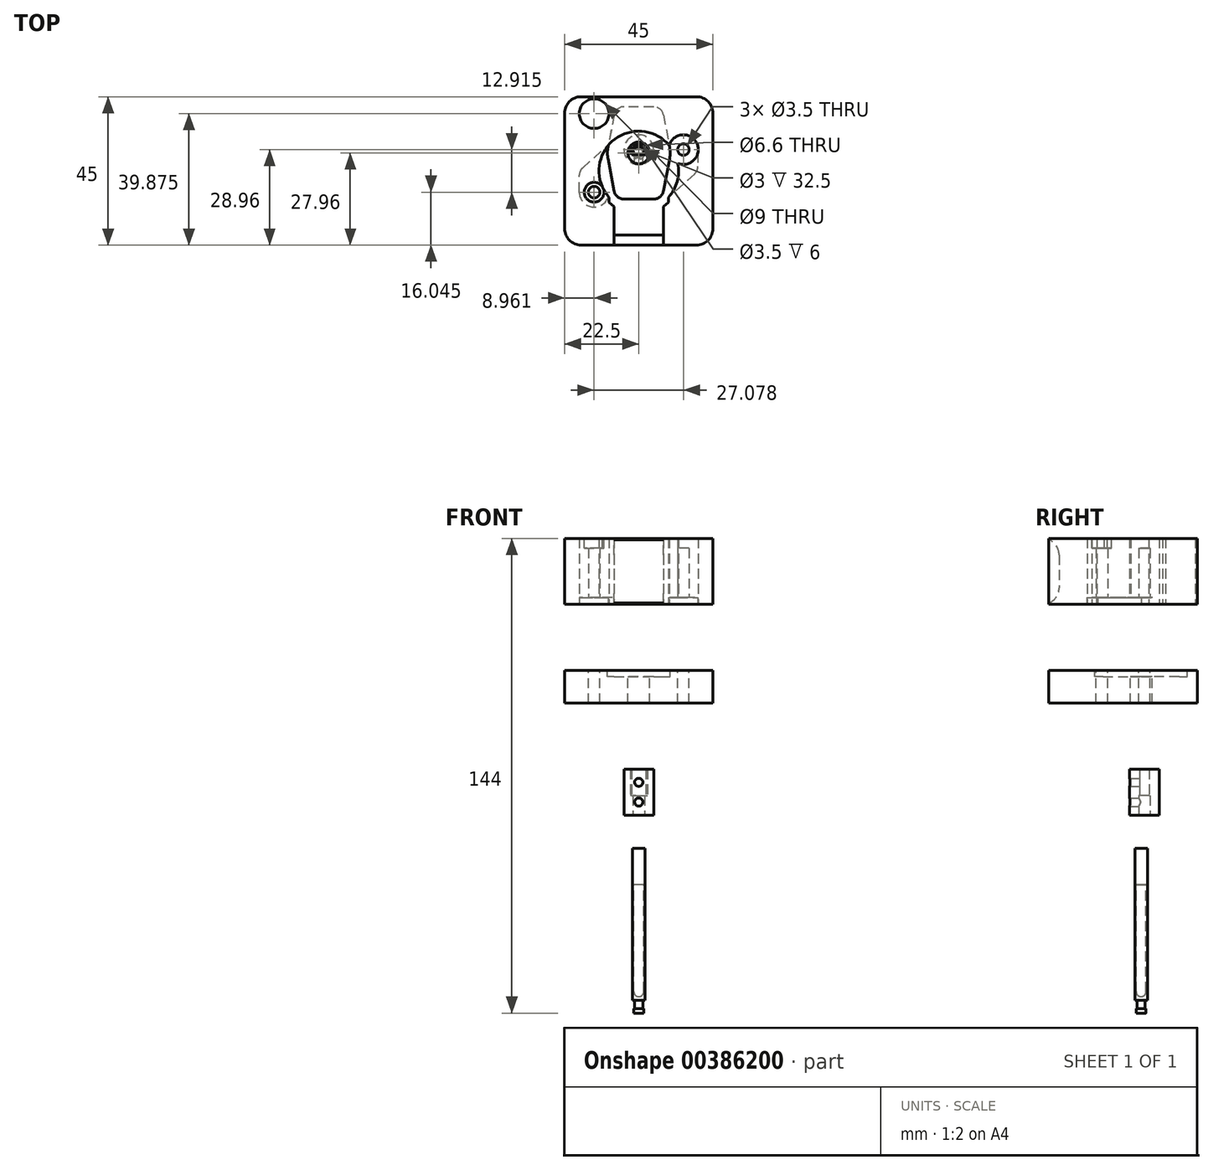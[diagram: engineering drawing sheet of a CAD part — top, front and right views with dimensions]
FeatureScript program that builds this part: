
annotation { "Feature Type Name" : "Feature", "Feature Type Description" : "" }
export const myFeature = defineFeature(function(context is Context, id is Id, definition is map)
    precondition{}
    {
        {
            assignVariable(context, id + "F0", {"name" : "plunger_h", "anyValue" : 50});
        }
        {
            assignVariable(context, id + "F1", {"name" : "M4_rivet_len", "anyValue" : 11});
        }
        {
            var Q0;
            Q0=qCreatedBy(makeId("Front.planeOp"),FACE);
            var sketch = newSketch(context, id + "F2", { "sketchPlane" : qUnion([Q0])});
            skLineSegment(sketch, "E0", {"start": v(0, 15.38) * mm, "end": v(0, -12.78) * mm, "construction": true});
            skLineSegment(sketch, "E1", {"start": v(0, 0) * mm, "end": v(1.5, 0) * mm});
            skLineSegment(sketch, "E2", {"start": v(1.5, 0) * mm, "end": v(1.5, 1.4) * mm});
            skLineSegment(sketch, "E3", {"start": v(1.5, 1.4) * mm, "end": v(1.25, 1.4) * mm});
            skLineSegment(sketch, "E4", {"start": v(1.25, 1.4) * mm, "end": v(1.25, 3.9) * mm});
            skLineSegment(sketch, "E5", {"start": v(1.25, 3.9) * mm, "end": v(1.9, 3.9) * mm});
            skLineSegment(sketch, "E6", {"start": v(1.9, 3.9) * mm, "end": v(1.9, 50) * mm});
            skLineSegment(sketch, "E7", {"start": v(1.9, 50) * mm, "end": v(1.5, 50) * mm});
            skLineSegment(sketch, "E8", {"start": v(1.5, 50) * mm, "end": v(1.5, 6.5) * mm});
            skLineSegment(sketch, "E9", {"start": v(0, 5) * mm, "end": v(0, 5) * mm});
            skLineSegment(sketch, "E10", {"start": v(0, 5) * mm, "end": v(0, 0) * mm});
            skPoint(sketch, "E11.visualSharp", {"position": v(1.5, 5) * mm});
            skArc(sketch, "E11.filletArc", {"start": v(0, 5) * mm, "mid": v(1.06, 5.44) * mm, "end": v(1.5, 6.5) * mm});
            skSolve(sketch);
        }
        {
            var Q0;
            Q0=makeQuery(id+"F2.imprint","IMPRINT",FACE,{"disambiguationData":[TD([[makeQuery(id+"F2.imprint","IMPRINT",EDGE,{"derivedFrom":sQuery(id+"F2.wireOp",EDGE,"E1")}),1.0]])]});
            var Q1;
            Q1=sQuery(id+"F2.wireOp",EDGE,"E0");
            revolve(context, id + "F3", {"entities" : qUnion([Q0]), "axis" : qUnion([Q1]), "revolveType" : RevolveType.FULL});
        }
        {
            var Q0;
            Q0=makeQuery(id+"F3.opRevolve","SWEPT_FACE",FACE,{"disambiguationData":[OSD([sQuery(id+"F2.wireOp",EDGE,"E7")])]});
            var sketch = newSketch(context, id + "F4", { "sketchPlane" : qUnion([Q0])});
            skCircle(sketch, "E12", {"center": v(0, 0) * mm, "radius": 1.5 * mm});
            skLineSegment(sketch, "E13", {"start": v(0, 11.62) * mm, "end": v(0, -12.28) * mm, "construction": true});
            skLineSegment(sketch, "E14", {"start": v(11.89, 0) * mm, "end": v(-13.02, 0) * mm, "construction": true});
            skCircle(sketch, "E15", {"center": v(0, 1) * mm, "radius": 1.75 * mm});
            skSolve(sketch);
        }
        {
            var Q0;
            Q0=makeQuery(id+"F4.imprint","IMPRINT",FACE,{"disambiguationData":[TD([[makeQuery(id+"F4.imprint","IMPRINT",EDGE,{"derivedFrom":sQuery(id+"F4.wireOp",EDGE,"E12")}),1.0]])]});
            extrude(context, id + "F5", {"entities" : qUnion([Q0]), "operationType" : NewBodyOperationType.ADD, "oppositeDirection" : true, "depth" : (getVariable(context, 'M4_rivet_len')) * mm});
        }
        {
            var Q0;
            Q0=qCreatedBy(makeId("Top.planeOp"),FACE);
            cPlane(context, id + "F6", {"entities" : qUnion([Q0]), "cplaneType" : CPlaneType.OFFSET, "offset" : (getVariable(context, 'plunger_h') + 10) * mm, "width" : 150 * mm, "height" : 150 * mm});
        }
        {
            var Q0;
            Q0=qCreatedBy(id+"F6.planeOp",FACE);
            var sketch = newSketch(context, id + "F7", { "sketchPlane" : qUnion([Q0])});
            skCircle(sketch, "E16", {"center": v(0, 1) * mm, "radius": 4.5 * mm});
            skCircle(sketch, "E17", {"center": v(0, 1) * mm, "radius": 2.6 * mm});
            skLineSegment(sketch, "E18", {"start": v(-2.12, 2.5) * mm, "end": v(2.12, 2.5) * mm});
            skLineSegment(sketch, "E19", {"start": v(-2.12, -0.5) * mm, "end": v(2.12, -0.5) * mm});
            skCircle(sketch, "E20", {"center": v(0, 1) * mm, "radius": 1.75 * mm});
            skSolve(sketch);
        }
        {
            var Q0;
            Q0=makeQuery(id+"F7.imprint","IMPRINT",FACE,{"disambiguationData":[TD([[makeQuery(id+"F7.imprint","IMPRINT",EDGE,{"derivedFrom":sQuery(id+"F7.wireOp",EDGE,"E16")}),1.0]])]});
            var Q1;
            {var subQ0=sQuery(id+"F7.wireOp",EDGE,"E19");var subQ1=sQuery(id+"F7.wireOp",EDGE,"E17");var subQ2=makeQuery(id+"F7.imprint","INTERSECT",VERTEX,{"disambiguationData":[OD(0.0)],"derivedFrom":[subQ1,subQ0]});Q1=makeQuery(id+"F7.imprint","IMPRINT",FACE,{"disambiguationData":[TD([[makeQuery(id+"F7.imprint","IMPRINT",EDGE,{"disambiguationData":[TD([[subQ2,-1.0]])],"derivedFrom":subQ1}),1.0]])]});}
            var Q2;
            {var subQ0=sQuery(id+"F7.wireOp",EDGE,"E20");var subQ1=sQuery(id+"F7.wireOp",EDGE,"E18");var subQ2=makeQuery(id+"F7.imprint","INTERSECT",VERTEX,{"disambiguationData":[OD(0.0)],"derivedFrom":[subQ1,subQ0]});Q2=makeQuery(id+"F7.imprint","IMPRINT",FACE,{"disambiguationData":[TD([[makeQuery(id+"F7.imprint","IMPRINT",EDGE,{"disambiguationData":[TD([[subQ2,-1.0]])],"derivedFrom":subQ1}),1.0]])]});}
            var Q3;
            {var subQ0=sQuery(id+"F7.wireOp",EDGE,"E20");var subQ1=sQuery(id+"F7.wireOp",EDGE,"E19");var subQ2=makeQuery(id+"F7.imprint","INTERSECT",VERTEX,{"disambiguationData":[OD(0.0)],"derivedFrom":[subQ1,subQ0]});Q3=makeQuery(id+"F7.imprint","IMPRINT",FACE,{"disambiguationData":[TD([[makeQuery(id+"F7.imprint","IMPRINT",EDGE,{"disambiguationData":[TD([[subQ2,-1.0]])],"derivedFrom":subQ1}),-1.0]])]});}
            var Q4;
            {var subQ0=sQuery(id+"F7.wireOp",EDGE,"E18");var subQ1=sQuery(id+"F7.wireOp",EDGE,"E17");var subQ2=makeQuery(id+"F7.imprint","INTERSECT",VERTEX,{"disambiguationData":[OD(0.0)],"derivedFrom":[subQ1,subQ0]});Q4=makeQuery(id+"F7.imprint","IMPRINT",FACE,{"disambiguationData":[TD([[makeQuery(id+"F7.imprint","IMPRINT",EDGE,{"disambiguationData":[TD([[subQ2,1.0]])],"derivedFrom":subQ1}),1.0]])]});}
            extrude(context, id + "F8", {"entities" : qUnion([Q0, Q1, Q2, Q3, Q4]), "depth" : 14 * mm});
        }
        {
            var Q0;
            {var subQ0=sQuery(id+"F7.wireOp",EDGE,"E18");var subQ1=sQuery(id+"F7.wireOp",EDGE,"E17");var subQ2=makeQuery(id+"F7.imprint","INTERSECT",VERTEX,{"disambiguationData":[OD(0.0)],"derivedFrom":[subQ1,subQ0]});Q0=makeQuery(id+"F7.imprint","IMPRINT",FACE,{"disambiguationData":[TD([[makeQuery(id+"F7.imprint","IMPRINT",EDGE,{"disambiguationData":[TD([[subQ2,-1.0]])],"derivedFrom":subQ1}),1.0]])]});}
            var Q1;
            {var subQ0=sQuery(id+"F7.wireOp",EDGE,"E18");var subQ1=sQuery(id+"F7.wireOp",EDGE,"E17");var subQ2=makeQuery(id+"F7.imprint","INTERSECT",VERTEX,{"disambiguationData":[OD(1.0)],"derivedFrom":[subQ1,subQ0]});Q1=makeQuery(id+"F7.imprint","IMPRINT",FACE,{"disambiguationData":[TD([[makeQuery(id+"F7.imprint","IMPRINT",EDGE,{"disambiguationData":[TD([[subQ2,1.0]])],"derivedFrom":subQ1}),1.0]])]});}
            extrude(context, id + "F9", {"entities" : qUnion([Q0, Q1]), "operationType" : NewBodyOperationType.ADD, "depth" : 6 * mm});
        }
        {
            var Q0;
            {var subQ0=sQuery(id+"F7.wireOp",EDGE,"E20");var subQ1=sQuery(id+"F7.wireOp",EDGE,"E18");var subQ2=makeQuery(id+"F7.imprint","INTERSECT",VERTEX,{"disambiguationData":[OD(0.0)],"derivedFrom":[subQ1,subQ0]});Q0=makeQuery(id+"F7.imprint","IMPRINT",FACE,{"disambiguationData":[TD([[makeQuery(id+"F7.imprint","IMPRINT",EDGE,{"disambiguationData":[TD([[subQ2,-1.0]])],"derivedFrom":subQ1}),1.0]])]});}
            var Q1;
            {var subQ0=sQuery(id+"F7.wireOp",EDGE,"E20");var subQ1=sQuery(id+"F7.wireOp",EDGE,"E19");var subQ2=makeQuery(id+"F7.imprint","INTERSECT",VERTEX,{"disambiguationData":[OD(0.0)],"derivedFrom":[subQ1,subQ0]});Q1=makeQuery(id+"F7.imprint","IMPRINT",FACE,{"disambiguationData":[TD([[makeQuery(id+"F7.imprint","IMPRINT",EDGE,{"disambiguationData":[TD([[subQ2,-1.0]])],"derivedFrom":subQ1}),-1.0]])]});}
            extrude(context, id + "F10", {"entities" : qUnion([Q0, Q1]), "operationType" : NewBodyOperationType.REMOVE, "depth" : 6 * mm});
        }
        {
            var Q0;
            Q0=makeQuery(id+"F8.opExtrude","CAP_FACE",FACE,{"disambiguationData":[OSD([sQuery(id+"F7.wireOp",EDGE,"E16"),sQuery(id+"F7.wireOp",EDGE,"E17"),sQuery(id+"F7.wireOp",EDGE,"E18"),sQuery(id+"F7.wireOp",EDGE,"E19")])],"isStart":false});
            cPlane(context, id + "F11", {"entities" : qUnion([Q0]), "cplaneType" : CPlaneType.OFFSET, "offset" : 50 * mm, "width" : 150 * mm, "height" : 150 * mm});
        }
        {
            var Q0;
            Q0=qCreatedBy(id+"F11.planeOp",FACE);
            var sketch = newSketch(context, id + "F12", { "sketchPlane" : qUnion([Q0])});
            skLineSegment(sketch, "E21", {"start": v(0, -36.46) * mm, "end": v(0, 8.54) * mm, "construction": true});
            skArc(sketch, "E22", {"start": v(7.5, -14.89) * mm, "mid": v(0, 6.6) * mm, "end": v(-7.5, -14.89) * mm});
            skLineSegment(sketch, "E23.top", {"start": v(-7.5, -24.89) * mm, "end": v(7.5, -24.89) * mm});
            skLineSegment(sketch, "E23.left", {"start": v(-7.5, -14.89) * mm, "end": v(-7.5, -24.89) * mm});
            skLineSegment(sketch, "E23.right", {"start": v(7.5, -14.89) * mm, "end": v(7.5, -24.89) * mm});
            skLineSegment(sketch, "E24", {"start": v(-28.87, -5.46) * mm, "end": v(25.7, -5.46) * mm, "construction": true});
            skCircle(sketch, "E25", {"center": v(-13.54, -11.92) * mm, "radius": 1.75 * mm});
            skLineSegment(sketch, "E26", {"start": v(21.88, 4.98) * mm, "end": v(-18.35, -14.21) * mm, "construction": true});
            skLineSegment(sketch, "E27", {"start": v(-2.48, -0.26) * mm, "end": v(2.36, -10.4) * mm, "construction": true});
            skCircle(sketch, "E28.MirrorC", {"center": v(13.54, 1) * mm, "radius": 1.75 * mm});
            skCircle(sketch, "E29", {"center": v(-13.54, -11.92) * mm, "radius": 4.5 * mm});
            skCircle(sketch, "E30.MirrorC", {"center": v(13.54, 1) * mm, "radius": 4.5 * mm});
            skLineSegment(sketch, "E31", {"start": v(-13.54, 1) * mm, "end": v(16.76, 1) * mm, "construction": true});
            skLineSegment(sketch, "E32.bottom", {"start": v(-22.5, -27.96) * mm, "end": v(22.5, -27.96) * mm});
            skLineSegment(sketch, "E32.top", {"start": v(-22.5, 17.04) * mm, "end": v(22.5, 17.04) * mm});
            skLineSegment(sketch, "E32.left", {"start": v(-22.5, -27.96) * mm, "end": v(-22.5, 17.04) * mm});
            skLineSegment(sketch, "E32.right", {"start": v(22.5, -27.96) * mm, "end": v(22.5, 17.04) * mm});
            skLineSegment(sketch, "E33", {"start": v(17.93, 0) * mm, "end": v(17.93, -5.46) * mm});
            skLineSegment(sketch, "E34", {"start": v(17.93, -5.46) * mm, "end": v(8.1, -14.38) * mm});
            skLineSegment(sketch, "E35", {"start": v(-18.04, -11.92) * mm, "end": v(-18.04, -5.46) * mm});
            skLineSegment(sketch, "E36", {"start": v(-18.04, -5.46) * mm, "end": v(-8.05, 3.5) * mm});
            skLineSegment(sketch, "E37", {"start": v(7.5, -16.33) * mm, "end": v(9, -14.97) * mm});
            skLineSegment(sketch, "E38", {"start": v(9, -14.97) * mm, "end": v(9, -13.47) * mm});
            skLineSegment(sketch, "E39.MirrorCS", {"start": v(-9, -14.97) * mm, "end": v(-9, -13.47) * mm});
            skLineSegment(sketch, "E40.MirrorCS", {"start": v(-7.5, -16.33) * mm, "end": v(-9, -14.97) * mm});
            skCircle(sketch, "E41.MirrorC", {"center": v(-13.54, 11.92) * mm, "radius": 4.5 * mm});
            skCircle(sketch, "E42.MirrorC", {"center": v(-13.54, 11.92) * mm, "radius": 1.75 * mm});
            skSolve(sketch);
        }
        {
            var Q0;
            Q0=makeQuery(id+"F12.imprint","IMPRINT",FACE,{"disambiguationData":[TD([[makeQuery(id+"F12.imprint","IMPRINT",EDGE,{"derivedFrom":sQuery(id+"F12.wireOp",EDGE,"E23.top")}),-1.0]])]});
            var Q1;
            Q1=makeQuery(id+"F12.imprint","IMPRINT",FACE,{"disambiguationData":[TD([[makeQuery(id+"F12.imprint","IMPRINT",EDGE,{"derivedFrom":sQuery(id+"F12.wireOp",EDGE,"E25")}),-1.0]])]});
            var Q2;
            Q2=makeQuery(id+"F12.imprint","IMPRINT",FACE,{"disambiguationData":[TD([[makeQuery(id+"F12.imprint","IMPRINT",EDGE,{"derivedFrom":sQuery(id+"F12.wireOp",EDGE,"E28.MirrorC")}),1.0]])]});
            var Q3;
            {var subQ0=sQuery(id+"F12.wireOp",EDGE,"k2Qoqp3b-hXQt-jHLW-PKsZ-R2O1SkHAnaxJ");Q3=makeQuery(id+"F12.imprint","IMPRINT",FACE,{"disambiguationData":[TD([[makeQuery(id+"F12.imprint","IMPRINT",EDGE,{"derivedFrom":subQ0}),-1.0]])]});}
            var Q4;
            {var subQ0=sQuery(id+"F12.wireOp",EDGE,"wLy7N8RW-QBpT-u1sk-OffF-8t74B9jOru9W");Q4=makeQuery(id+"F12.imprint","IMPRINT",FACE,{"disambiguationData":[TD([[makeQuery(id+"F12.imprint","IMPRINT",EDGE,{"derivedFrom":subQ0}),1.0]])]});}
            var Q5;
            {var subQ4=sQuery(id+"F12.wireOp",EDGE,"E33");Q5=makeQuery(id+"F12.imprint","IMPRINT",FACE,{"disambiguationData":[TD([[makeQuery(id+"F12.imprint","IMPRINT",EDGE,{"derivedFrom":subQ4}),-1.0]])]});}
            var Q6;
            {var subQ4=sQuery(id+"F12.wireOp",EDGE,"E35");Q6=makeQuery(id+"F12.imprint","IMPRINT",FACE,{"disambiguationData":[TD([[makeQuery(id+"F12.imprint","IMPRINT",EDGE,{"derivedFrom":subQ4}),-1.0]])]});}
            var Q7;
            Q7=makeQuery(id+"F12.imprint","IMPRINT",FACE,{"disambiguationData":[TD([[makeQuery(id+"F12.imprint","IMPRINT",EDGE,{"derivedFrom":sQuery(id+"F12.wireOp",EDGE,"E41.MirrorC")}),-1.0]])]});
            extrude(context, id + "F13", {"entities" : qUnion([Q0, Q1, Q2, Q3, Q4, Q5, Q6, Q7]), "depth" : 20 * mm});
        }
        {
            var Q0;
            Q0=makeQuery(id+"F13.opExtrude","CAP_FACE",FACE,{"disambiguationData":[OSD([sQuery(id+"F12.wireOp",EDGE,"E22"),sQuery(id+"F12.wireOp",EDGE,"E23.top"),sQuery(id+"F12.wireOp",EDGE,"E23.left"),sQuery(id+"F12.wireOp",EDGE,"E23.right"),sQuery(id+"F12.wireOp",EDGE,"E25"),sQuery(id+"F12.wireOp",EDGE,"E28.MirrorC"),sQuery(id+"F12.wireOp",EDGE,"E32.bottom"),sQuery(id+"F12.wireOp",EDGE,"E32.top"),sQuery(id+"F12.wireOp",EDGE,"E32.left"),sQuery(id+"F12.wireOp",EDGE,"E32.right")])],"isStart":true});
            cPlane(context, id + "F14", {"entities" : qUnion([Q0]), "cplaneType" : CPlaneType.OFFSET, "offset" : 20 * mm, "width" : 150 * mm, "height" : 150 * mm});
        }
        {
            var Q0;
            Q0=qCreatedBy(id+"F14.planeOp",FACE);
            var sketch = newSketch(context, id + "F15", { "sketchPlane" : qUnion([Q0])});
            skLineSegment(sketch, "E43.bottom", {"start": v(-22.5, -17.04) * mm, "end": v(22.5, -17.04) * mm});
            skLineSegment(sketch, "E43.top", {"start": v(-22.5, 27.96) * mm, "end": v(22.5, 27.96) * mm});
            skLineSegment(sketch, "E43.left", {"start": v(-22.5, -17.04) * mm, "end": v(-22.5, 27.96) * mm});
            skLineSegment(sketch, "E43.right", {"start": v(22.5, -17.04) * mm, "end": v(22.5, 27.96) * mm});
            skCircle(sketch, "E44", {"center": v(0, 0) * mm, "radius": 3.3 * mm});
            skCircle(sketch, "E45", {"center": v(-13.54, 11.92) * mm, "radius": 1.75 * mm});
            skCircle(sketch, "E46", {"center": v(13.54, -1) * mm, "radius": 1.75 * mm});
            skCircle(sketch, "E47", {"center": v(0, 0) * mm, "radius": 9.5 * mm});
            skLineSegment(sketch, "E48", {"start": v(0, 14) * mm, "end": v(4.52, 14) * mm});
            skLineSegment(sketch, "E49", {"start": v(7.47, 11.56) * mm, "end": v(9.33, 1.78) * mm});
            skPoint(sketch, "E50.visualSharp", {"position": v(7, 14) * mm});
            skArc(sketch, "E50.filletArc", {"start": v(7.47, 11.56) * mm, "mid": v(6.43, 13.31) * mm, "end": v(4.52, 14) * mm});
            skLineSegment(sketch, "E51.MirrorCS", {"start": v(0, 14) * mm, "end": v(-4.52, 14) * mm});
            skArc(sketch, "E52.MirrorCS", {"start": v(-7.47, 11.56) * mm, "mid": v(-6.43, 13.31) * mm, "end": v(-4.52, 14) * mm});
            skLineSegment(sketch, "E53.MirrorCS", {"start": v(-7.47, 11.56) * mm, "end": v(-9.33, 1.78) * mm});
            skLineSegment(sketch, "E54.MirrorCS", {"start": v(-7.47, -11.56) * mm, "end": v(-9.33, -1.78) * mm});
            skArc(sketch, "E55.MirrorCS", {"start": v(-7.47, -11.56) * mm, "mid": v(-6.43, -13.31) * mm, "end": v(-4.52, -14) * mm});
            skLineSegment(sketch, "E56.MirrorCS", {"start": v(0, -14) * mm, "end": v(4.52, -14) * mm});
            skLineSegment(sketch, "E57.MirrorCS", {"start": v(0, -14) * mm, "end": v(-4.52, -14) * mm});
            skArc(sketch, "E58.MirrorCS", {"start": v(7.47, -11.56) * mm, "mid": v(6.43, -13.31) * mm, "end": v(4.52, -14) * mm});
            skLineSegment(sketch, "E59.MirrorCS", {"start": v(7.47, -11.56) * mm, "end": v(9.33, -1.78) * mm});
            skSolve(sketch);
        }
        {
            var Q0;
            Q0=makeQuery(id+"F15.imprint","IMPRINT",FACE,{"disambiguationData":[TD([[makeQuery(id+"F15.imprint","IMPRINT",EDGE,{"derivedFrom":sQuery(id+"F15.wireOp",EDGE,"E43.bottom")}),1.0]])]});
            var Q1;
            {var subQ0=sQuery(id+"F15.wireOp",EDGE,"E54.MirrorCS");Q1=makeQuery(id+"F15.imprint","IMPRINT",FACE,{"disambiguationData":[TD([[makeQuery(id+"F15.imprint","IMPRINT",EDGE,{"derivedFrom":subQ0}),-1.0]])]});}
            var Q2;
            Q2=makeQuery(id+"F15.imprint","IMPRINT",FACE,{"disambiguationData":[TD([[makeQuery(id+"F15.imprint","IMPRINT",EDGE,{"derivedFrom":sQuery(id+"F15.wireOp",EDGE,"E48")}),-1.0]])]});
            var Q3;
            Q3=makeQuery(id+"F15.imprint","IMPRINT",FACE,{"disambiguationData":[TD([[makeQuery(id+"F15.imprint","IMPRINT",EDGE,{"derivedFrom":sQuery(id+"F15.wireOp",EDGE,"E44")}),-1.0]])]});
            extrude(context, id + "F16", {"entities" : qUnion([Q0, Q1, Q2, Q3]), "depth" : 10 * mm});
        }
        {
            var Q0;
            {var subQ0=sQuery(id+"F15.wireOp",EDGE,"E54.MirrorCS");Q0=makeQuery(id+"F15.imprint","IMPRINT",FACE,{"disambiguationData":[TD([[makeQuery(id+"F15.imprint","IMPRINT",EDGE,{"derivedFrom":subQ0}),-1.0]])]});}
            var Q1;
            Q1=makeQuery(id+"F15.imprint","IMPRINT",FACE,{"disambiguationData":[TD([[makeQuery(id+"F15.imprint","IMPRINT",EDGE,{"derivedFrom":sQuery(id+"F15.wireOp",EDGE,"E48")}),-1.0]])]});
            var Q2;
            Q2=makeQuery(id+"F15.imprint","IMPRINT",FACE,{"disambiguationData":[TD([[makeQuery(id+"F15.imprint","IMPRINT",EDGE,{"derivedFrom":sQuery(id+"F15.wireOp",EDGE,"E44")}),-1.0]])]});
            extrude(context, id + "F17", {"entities" : qUnion([Q0, Q1, Q2]), "operationType" : NewBodyOperationType.REMOVE, "depth" : 2 * mm});
        }
        {
            var Q0;
            {var subQ0=sQuery(id+"F12.wireOp",EDGE,"wLy7N8RW-QBpT-u1sk-OffF-8t74B9jOru9W");Q0=makeQuery(id+"F12.imprint","IMPRINT",FACE,{"disambiguationData":[TD([[makeQuery(id+"F12.imprint","IMPRINT",EDGE,{"derivedFrom":subQ0}),1.0]])]});}
            var Q1;
            Q1=makeQuery(id+"F12.imprint","IMPRINT",FACE,{"disambiguationData":[TD([[makeQuery(id+"F12.imprint","IMPRINT",EDGE,{"derivedFrom":sQuery(id+"F12.wireOp",EDGE,"E28.MirrorC")}),1.0]])]});
            var Q2;
            {var subQ0=sQuery(id+"F12.wireOp",EDGE,"k2Qoqp3b-hXQt-jHLW-PKsZ-R2O1SkHAnaxJ");Q2=makeQuery(id+"F12.imprint","IMPRINT",FACE,{"disambiguationData":[TD([[makeQuery(id+"F12.imprint","IMPRINT",EDGE,{"derivedFrom":subQ0}),-1.0]])]});}
            var Q3;
            Q3=makeQuery(id+"F12.imprint","IMPRINT",FACE,{"disambiguationData":[TD([[makeQuery(id+"F12.imprint","IMPRINT",EDGE,{"derivedFrom":sQuery(id+"F12.wireOp",EDGE,"E25")}),-1.0]])]});
            var Q4;
            {var subQ4=sQuery(id+"F12.wireOp",EDGE,"E35");Q4=makeQuery(id+"F12.imprint","IMPRINT",FACE,{"disambiguationData":[TD([[makeQuery(id+"F12.imprint","IMPRINT",EDGE,{"derivedFrom":subQ4}),-1.0]])]});}
            var Q5;
            {var subQ4=sQuery(id+"F12.wireOp",EDGE,"E33");Q5=makeQuery(id+"F12.imprint","IMPRINT",FACE,{"disambiguationData":[TD([[makeQuery(id+"F12.imprint","IMPRINT",EDGE,{"derivedFrom":subQ4}),-1.0]])]});}
            extrude(context, id + "F18", {"entities" : qUnion([Q0, Q1, Q2, Q3, Q4, Q5]), "operationType" : NewBodyOperationType.REMOVE, "depth" : 2 * mm});
        }
        {
            var Q0;
            Q0=makeQuery(id+"F13.opExtrude","SWEPT_EDGE",EDGE,{"disambiguationData":[OSD([sQuery(id+"F12.wireOp",EDGE,"E32.top"),sQuery(id+"F12.wireOp",EDGE,"E32.right")])]});
            var Q1;
            Q1=makeQuery(id+"F16.opExtrude","SWEPT_EDGE",EDGE,{"disambiguationData":[OSD([sQuery(id+"F15.wireOp",EDGE,"E43.bottom"),sQuery(id+"F15.wireOp",EDGE,"E43.right")])]});
            var Q2;
            Q2=makeQuery(id+"F16.opExtrude","SWEPT_EDGE",EDGE,{"disambiguationData":[OSD([sQuery(id+"F15.wireOp",EDGE,"E43.bottom"),sQuery(id+"F15.wireOp",EDGE,"E43.left")])]});
            var Q3;
            Q3=makeQuery(id+"F13.opExtrude","SWEPT_EDGE",EDGE,{"disambiguationData":[OSD([sQuery(id+"F12.wireOp",EDGE,"E32.top"),sQuery(id+"F12.wireOp",EDGE,"E32.left")])]});
            var Q4;
            Q4=makeQuery(id+"F16.opExtrude","SWEPT_EDGE",EDGE,{"disambiguationData":[OSD([sQuery(id+"F15.wireOp",EDGE,"E43.top"),sQuery(id+"F15.wireOp",EDGE,"E43.left")])]});
            var Q5;
            Q5=makeQuery(id+"F13.opExtrude","SWEPT_EDGE",EDGE,{"disambiguationData":[OSD([sQuery(id+"F12.wireOp",EDGE,"E32.bottom"),sQuery(id+"F12.wireOp",EDGE,"E32.left")])]});
            var Q6;
            Q6=makeQuery(id+"F16.opExtrude","SWEPT_EDGE",EDGE,{"disambiguationData":[OSD([sQuery(id+"F15.wireOp",EDGE,"E43.top"),sQuery(id+"F15.wireOp",EDGE,"E43.right")])]});
            var Q7;
            Q7=makeQuery(id+"F13.opExtrude","SWEPT_EDGE",EDGE,{"disambiguationData":[OSD([sQuery(id+"F12.wireOp",EDGE,"E32.bottom"),sQuery(id+"F12.wireOp",EDGE,"E32.right")])]});
            fillet(context, id + "F19", {"entities" : qUnion([Q0, Q1, Q2, Q3, Q4, Q5, Q6, Q7]), "radius" : 5 * mm, "tangentPropagation" : true, "allowEdgeOverflow" : false});
        }
        {
            var Q0;
            Q0=makeQuery(id+"F18.boolean.opBoolean","COPY",EDGE,{"derivedFrom":makeQuery(id+"F18.opExtrude","SWEPT_EDGE",EDGE,{"disambiguationData":[OSD([sQuery(id+"F12.wireOp",EDGE,"E33"),sQuery(id+"F12.wireOp",EDGE,"E34")])]})});
            var Q1;
            Q1=makeQuery(id+"F18.boolean.opBoolean","COPY",EDGE,{"derivedFrom":makeQuery(id+"F18.opExtrude","SWEPT_EDGE",EDGE,{"disambiguationData":[OSD([sQuery(id+"F12.wireOp",EDGE,"E35"),sQuery(id+"F12.wireOp",EDGE,"E36")])]})});
            fillet(context, id + "F20", {"entities" : qUnion([Q0, Q1]), "radius" : 3 * mm, "tangentPropagation" : true, "allowEdgeOverflow" : false});
        }
        {
            var Q0;
            Q0=makeQuery(id+"F13.opExtrude","CAP_EDGE",EDGE,{"disambiguationData":[OSD([sQuery(id+"F12.wireOp",EDGE,"E23.top")])],"isStart":false});
            fillet(context, id + "F21", {"entities" : qUnion([Q0]), "radius" : 5 * mm, "tangentPropagation" : true, "allowEdgeOverflow" : false});
        }
        {
            var Q0;
            Q0=makeQuery(id+"F13.opExtrude","CAP_EDGE",EDGE,{"disambiguationData":[OSD([sQuery(id+"F12.wireOp",EDGE,"E23.top")])],"isStart":true});
            fillet(context, id + "F22", {"entities" : qUnion([Q0]), "radius" : 5 * mm, "tangentPropagation" : true, "allowEdgeOverflow" : false});
        }
        {
            var Q0;
            Q0=qCreatedBy(makeId("Front.planeOp"),FACE);
            var sketch = newSketch(context, id + "F23", { "sketchPlane" : qUnion([Q0])});
            skCircle(sketch, "E60", {"center": v(0, 64) * mm, "radius": 1.25 * mm});
            skCircle(sketch, "E61", {"center": v(0, 70) * mm, "radius": 1.25 * mm});
            skSolve(sketch);
        }
        {
            var Q0;
            Q0=makeQuery(id+"F23.imprint","IMPRINT",FACE,{"disambiguationData":[TD([[makeQuery(id+"F23.imprint","IMPRINT",EDGE,{"derivedFrom":sQuery(id+"F23.wireOp",EDGE,"E61")}),1.0]])]});
            var Q1;
            Q1=makeQuery(id+"F23.imprint","IMPRINT",FACE,{"disambiguationData":[TD([[makeQuery(id+"F23.imprint","IMPRINT",EDGE,{"derivedFrom":sQuery(id+"F23.wireOp",EDGE,"E60")}),1.0]])]});
            var Q2;
            Q2=sQuery(id+"F23.wireOp",EDGE,"E61");
            var Q3;
            Q3=sQuery(id+"F23.wireOp",EDGE,"E60");
            extrude(context, id + "F24", {"entities" : qUnion([Q0, Q1]), "operationType" : NewBodyOperationType.REMOVE, "surfaceEntities" : qUnion([Q2, Q3]), "endBound" : BoundingType.THROUGH_ALL, "depth" : 25 * mm});
        }
        {
            var Q0;
            Q0=makeQuery(id+"F13.opExtrude","CAP_FACE",FACE,{"disambiguationData":[OSD([sQuery(id+"F12.wireOp",EDGE,"E22"),sQuery(id+"F12.wireOp",EDGE,"E23.top"),sQuery(id+"F12.wireOp",EDGE,"E23.left"),sQuery(id+"F12.wireOp",EDGE,"E23.right"),sQuery(id+"F12.wireOp",EDGE,"E25"),sQuery(id+"F12.wireOp",EDGE,"E28.MirrorC"),sQuery(id+"F12.wireOp",EDGE,"E32.bottom"),sQuery(id+"F12.wireOp",EDGE,"E32.top"),sQuery(id+"F12.wireOp",EDGE,"E32.left"),sQuery(id+"F12.wireOp",EDGE,"E32.right"),sQuery(id+"F12.wireOp",EDGE,"E37"),sQuery(id+"F12.wireOp",EDGE,"E38"),sQuery(id+"F12.wireOp",EDGE,"E39.MirrorCS"),sQuery(id+"F12.wireOp",EDGE,"E40.MirrorCS"),sQuery(id+"F12.wireOp",EDGE,"E42.MirrorC")])],"isStart":false});
            var sketch = newSketch(context, id + "F25", { "sketchPlane" : qUnion([Q0])});
            skCircle(sketch, "E62", {"center": v(-13.54, 11.92) * mm, "radius": 3 * mm});
            skCircle(sketch, "E63", {"center": v(-13.54, -11.92) * mm, "radius": 3 * mm});
            skCircle(sketch, "E64", {"center": v(13.54, 1) * mm, "radius": 3 * mm});
            skSolve(sketch);
        }
        {
            var Q0;
            Q0=qSketchRegion(id+"F25",true);
            extrude(context, id + "F26", {"entities" : qUnion([Q0]), "operationType" : NewBodyOperationType.REMOVE, "oppositeDirection" : true, "depth" : 3 * mm});
        }
    });
